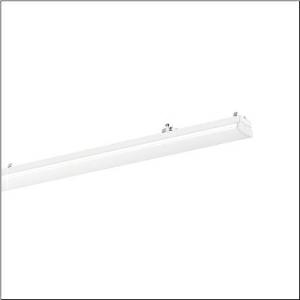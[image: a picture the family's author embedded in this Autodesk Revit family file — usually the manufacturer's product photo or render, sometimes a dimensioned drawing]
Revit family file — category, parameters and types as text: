
# Revit family: licross_r__11_recessed_opal_mo_51tl1ddv495g_cbeb
name_source: partatom
category: Lighting Fixtures
units: mm (PartAtom-declared; Revit-internal decimal feet)

## family parameters
Cut with Voids When Loaded = No
Host = Face
Light Source = No
Part Type = Normal
Room Calculation Point = No
Round Connector Dimension = Use Diameter
Shared = No

## types (1)
- --- (1 x LED, 9500 lm, 52.6 W, 4000K)
    Apparent Load = 53 VA
    CIE Flux Codes = 44 73 91 87 100
    Color Rendering = 80
    Color Temperature = 4000K
    Default Elevation = 1800 mm
    Description = Licross® 11 recessed opal MO, luminaire insert, of sheet steel, coil coated, white, length: 2.250mm, width: 76mm, height: 87mm, LED rated luminous flux: 9.500lm, light colour: 840, control gear: DALI 2, with plug, 5-pole, with phase selection, mains connection: 220..240V, AC, 50/60Hz, rated input power: 53W, internal wiring halogen-free, primary optical cover: cover, of PMMA, light emission: direct with ceiling illumination distribution, primary light characteristic: symmetric, protection rating (complete): IP40, insulation class (complete): insulation class I (protective earthing), certification: CE, ENEC, VDE, UKCA, protection symbol: D if used in an environment without relevant dust loads with corresponding accessories, impact resistance: IK06, permissible ambient temperature for indoor applications: -25..+40°C, corresponds to IFS (International Featured Standards) requirements for safety and quality in the food industry, reducing of maximum allowable ambient temperature of 5°C with ceiling mounting, LABS conformity tested according to VDMA 24364:2018-05, packaging unit: 1 piece
    Height = 83 mm
    Lamp = 1 x LED
    Lamp Light Flux = 9500 lm
    Lamp Power = 52.6 W
    Lamp count = 1
    Length = 2250 mm
    Luminous efficacy = 181 lm/W
    Manufacturer = Siteco
    ModVariant = No
    Model = 51TL1DDV495G
    Mounting Place = Ceiling
    Mounting Type = Pendant
    Number of Poles = 1
    OnlyDefault = Yes
    Power Factor = 1
    Product Name = Licross® 11 recessed opal MO
    Product group = luminaire insert | ceiling pendant
    ProductGroupID = 902
    Protection Class = Protection class I
    Protection Degree = IP 40
    RLX_Detail_Level = 1
    RLX_Emergency_Light_Flux = 0 lm
    RLX_Emergency_Type = 0
    RLX_Emergency_Type_DB = No
    RlxData = <blob elided: 26657 chars, md5=cdfc4a4f>
    Socket = socket
    Standby Power = 0 W
    System Light Flux = 9500 lm
    System Power = 53 W
    Type Comments = factory setting: luminous flux: 100 % | dim-lin: 254 | 239 mA
    Type Image = l_1313666.jpg
    URL = http://relux.com
    VarID = @adj_098035
    Voltage = 0 V
    Weight = 0.00 kg
    Width = 76 mm

## geometry (parser evidence)
native form markers: Blend x4, Sweep x12
no freeform markers — native parametric forms only
